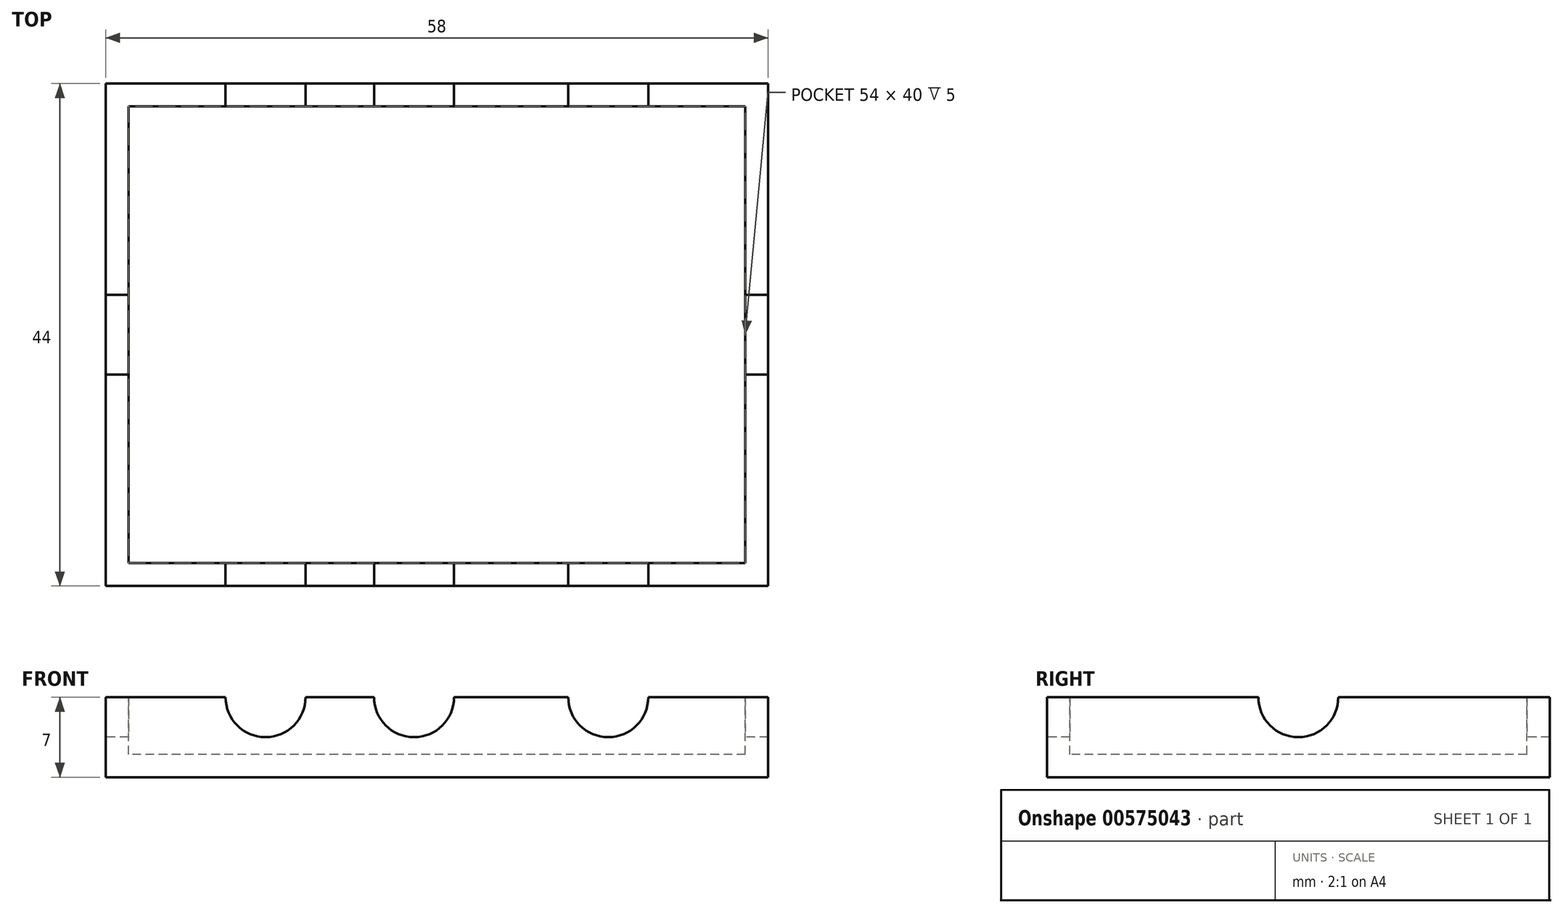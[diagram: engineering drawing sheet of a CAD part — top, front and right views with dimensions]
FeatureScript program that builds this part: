
annotation { "Feature Type Name" : "Feature", "Feature Type Description" : "" }
export const myFeature = defineFeature(function(context is Context, id is Id, definition is map)
    precondition{}
    {
        {
            var Q0;
            Q0=qCreatedBy(makeId("Top.planeOp"),FACE);
            var sketch = newSketch(context, id + "F0", { "sketchPlane" : qUnion([Q0])});
            skLineSegment(sketch, "E0.bottom", {"start": v(29, 22) * mm, "end": v(-29, 22) * mm});
            skLineSegment(sketch, "E0.top", {"start": v(29, -22) * mm, "end": v(-29, -22) * mm});
            skLineSegment(sketch, "E0.left", {"start": v(29, 22) * mm, "end": v(29, -22) * mm});
            skLineSegment(sketch, "E0.right", {"start": v(-29, 22) * mm, "end": v(-29, -22) * mm});
            skPoint(sketch, "E0.middle", {"position": v(0, 0) * mm});
            skSolve(sketch);
        }
        {
            var Q0;
            Q0 = qSketchRegion(id + "F0", true);
            extrude(context, id + "F1", {"entities" : qUnion([Q0]), "depth" : 7 * mm, "offsetDistance" : 25 * mm});
        }
        {
            var Q0;
            Q0=makeQuery(id+"F1.opExtrude","CAP_FACE",FACE,{"disambiguationData":[OSD([sQuery(id+"F0.wireOp",EDGE,"E0.bottom"),sQuery(id+"F0.wireOp",EDGE,"E0.top"),sQuery(id+"F0.wireOp",EDGE,"E0.left"),sQuery(id+"F0.wireOp",EDGE,"E0.right")])],"isStart":false});
            var sketch = newSketch(context, id + "F2", { "sketchPlane" : qUnion([Q0])});
            skLineSegment(sketch, "E1.bottom", {"start": v(27, 20) * mm, "end": v(-27, 20) * mm});
            skLineSegment(sketch, "E1.top", {"start": v(27, -20) * mm, "end": v(-27, -20) * mm});
            skLineSegment(sketch, "E1.left", {"start": v(27, 20) * mm, "end": v(27, -20) * mm});
            skLineSegment(sketch, "E1.right", {"start": v(-27, 20) * mm, "end": v(-27, -20) * mm});
            skPoint(sketch, "E1.middle", {"position": v(0, 0) * mm});
            skSolve(sketch);
        }
        {
            var Q0;
            Q0 = qSketchRegion(id + "F2", true);
            extrude(context, id + "F3", {"entities" : qUnion([Q0]), "operationType" : NewBodyOperationType.REMOVE, "oppositeDirection" : true, "depth" : 5 * mm, "offsetDistance" : 25 * mm});
        }
        {
            var Q0;
            Q0=makeQuery(id+"F1.opExtrude","SWEPT_FACE",FACE,{"disambiguationData":[OSD([sQuery(id+"F0.wireOp",EDGE,"E0.top")])]});
            var sketch = newSketch(context, id + "F4", { "sketchPlane" : qUnion([Q0])});
            skCircle(sketch, "E2", {"center": v(-15, 7) * mm, "radius": 3.5 * mm});
            skCircle(sketch, "E3", {"center": v(-2, 7) * mm, "radius": 3.5 * mm});
            skCircle(sketch, "E4", {"center": v(15, 7) * mm, "radius": 3.5 * mm});
            skSolve(sketch);
        }
        {
            var Q0;
            Q0 = qSketchRegion(id + "F4", true);
            extrude(context, id + "F5", {"entities" : qUnion([Q0]), "operationType" : NewBodyOperationType.REMOVE, "oppositeDirection" : true, "depth" : 50 * mm, "offsetDistance" : 25 * mm});
        }
        {
            var Q0;
            Q0=makeQuery(id+"F1.opExtrude","SWEPT_FACE",FACE,{"disambiguationData":[OSD([sQuery(id+"F0.wireOp",EDGE,"E0.right")])]});
            var sketch = newSketch(context, id + "F6", { "sketchPlane" : qUnion([Q0])});
            skCircle(sketch, "E5", {"center": v(0, 7) * mm, "radius": 3.5 * mm});
            skSolve(sketch);
        }
        {
            var Q0;
            Q0 = qSketchRegion(id + "F6", true);
            extrude(context, id + "F7", {"entities" : qUnion([Q0]), "operationType" : NewBodyOperationType.REMOVE, "oppositeDirection" : true, "depth" : 60 * mm, "offsetDistance" : 25 * mm});
        }
    });
